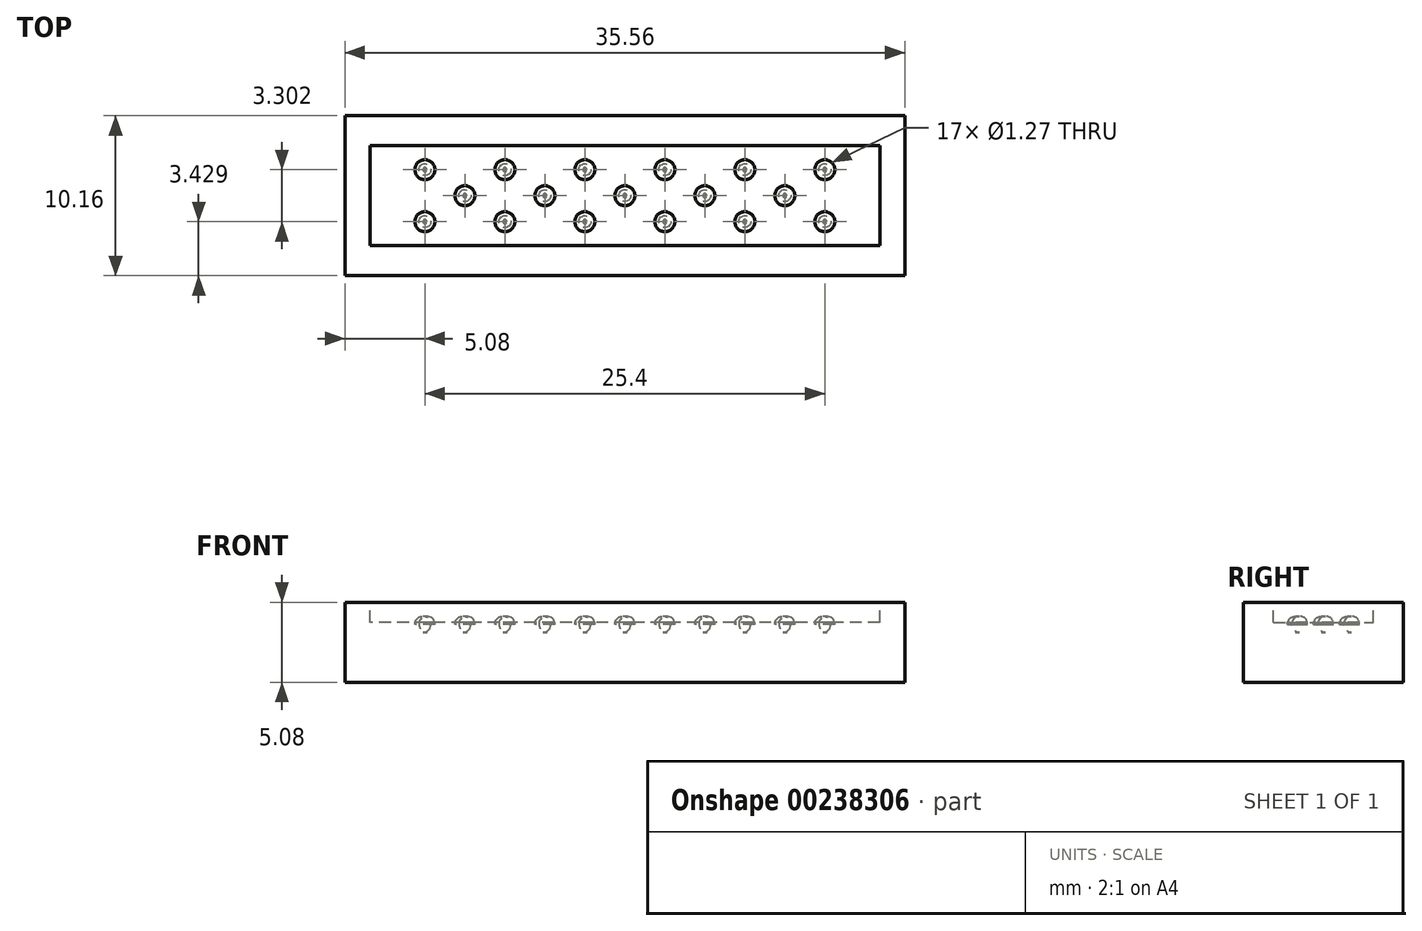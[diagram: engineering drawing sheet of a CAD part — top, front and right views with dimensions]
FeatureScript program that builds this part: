
annotation { "Feature Type Name" : "Feature", "Feature Type Description" : "" }
export const myFeature = defineFeature(function(context is Context, id is Id, definition is map)
    precondition{}
    {
        {
            var Q0;
            Q0=qCreatedBy(makeId("Top.planeOp"),FACE);
            var sketch = newSketch(context, id + "F0", { "sketchPlane" : qUnion([Q0])});
            skLineSegment(sketch, "E0.bottom", {"start": v(17.78, -5.08) * mm, "end": v(-17.78, -5.08) * mm});
            skLineSegment(sketch, "E0.top", {"start": v(17.78, 5.08) * mm, "end": v(-17.78, 5.08) * mm});
            skLineSegment(sketch, "E0.left", {"start": v(17.78, -5.08) * mm, "end": v(17.78, 5.08) * mm});
            skLineSegment(sketch, "E0.right", {"start": v(-17.78, -5.08) * mm, "end": v(-17.78, 5.08) * mm});
            skPoint(sketch, "E0.middle", {"position": v(0, 0) * mm});
            skSolve(sketch);
        }
        {
            var Q0;
            Q0=makeQuery(id+"F0.imprint","IMPRINT",FACE,{"disambiguationData":[TD([[makeQuery(id+"F0.imprint","IMPRINT",EDGE,{"derivedFrom":sQuery(id+"F0.wireOp",EDGE,"E0.bottom")}),-1.0]])]});
            extrude(context, id + "F1", {"entities" : qUnion([Q0]), "depth" : 5.08 * mm});
        }
        {
            var Q0;
            Q0=makeQuery(id+"F1.opExtrude","CAP_FACE",FACE,{"disambiguationData":[OSD([sQuery(id+"F0.wireOp",EDGE,"E0.bottom"),sQuery(id+"F0.wireOp",EDGE,"E0.top"),sQuery(id+"F0.wireOp",EDGE,"E0.left"),sQuery(id+"F0.wireOp",EDGE,"E0.right")])],"isStart":false});
            var sketch = newSketch(context, id + "F2", { "sketchPlane" : qUnion([Q0])});
            skLineSegment(sketch, "E1.bottom", {"start": v(16.2, -3.18) * mm, "end": v(-16.2, -3.18) * mm});
            skLineSegment(sketch, "E1.top", {"start": v(16.2, 3.18) * mm, "end": v(-16.2, 3.18) * mm});
            skLineSegment(sketch, "E1.left", {"start": v(16.2, -3.18) * mm, "end": v(16.2, 3.17) * mm});
            skLineSegment(sketch, "E1.right", {"start": v(-16.2, -3.18) * mm, "end": v(-16.2, 3.17) * mm});
            skPoint(sketch, "E1.middle", {"position": v(0, 0) * mm});
            skSolve(sketch);
        }
        {
            var Q0;
            Q0 = qSketchRegion(id + "F2", true);
            extrude(context, id + "F3", {"entities" : qUnion([Q0]), "operationType" : NewBodyOperationType.REMOVE, "oppositeDirection" : true, "depth" : 1.27 * mm});
        }
        {
            var Q0;
            Q0=makeQuery(id+"F3.boolean.opBoolean","COPY",FACE,{"derivedFrom":makeQuery(id+"F3.opExtrude","CAP_FACE",FACE,{"disambiguationData":[OSD([sQuery(id+"F2.wireOp",EDGE,"E1.bottom"),sQuery(id+"F2.wireOp",EDGE,"E1.top"),sQuery(id+"F2.wireOp",EDGE,"E1.left"),sQuery(id+"F2.wireOp",EDGE,"E1.right")])],"isStart":false})});
            var sketch = newSketch(context, id + "F4", { "sketchPlane" : qUnion([Q0])});
            skCircle(sketch, "E2", {"center": v(-12.7, 1.65) * mm, "radius": 0.64 * mm});
            skCircle(sketch, "E3", {"center": v(-10.16, 0) * mm, "radius": 0.64 * mm});
            skCircle(sketch, "E4.1.0.0", {"center": v(-7.62, 1.65) * mm, "radius": 0.64 * mm});
            skCircle(sketch, "E4.2.0.0", {"center": v(-2.54, 1.65) * mm, "radius": 0.64 * mm});
            skCircle(sketch, "E4.3.0.0", {"center": v(2.54, 1.65) * mm, "radius": 0.64 * mm});
            skCircle(sketch, "E4.4.0.0", {"center": v(7.62, 1.65) * mm, "radius": 0.64 * mm});
            skCircle(sketch, "E4.5.0.0", {"center": v(12.7, 1.65) * mm, "radius": 0.64 * mm});
            skLineSegment(sketch, "E4.direction1", {"start": v(-12.7, 1.65) * mm, "end": v(-7.62, 1.65) * mm, "construction": true});
            skLineSegment(sketch, "E5", {"start": v(-2.54, 1.65) * mm, "end": v(2.54, 1.65) * mm, "construction": true});
            skPoint(sketch, "E6", {"position": v(0, 1.65) * mm});
            skCircle(sketch, "E7.1.0.0", {"center": v(-5.08, 0) * mm, "radius": 0.64 * mm});
            skCircle(sketch, "E7.2.0.0", {"center": v(0, 0) * mm, "radius": 0.64 * mm});
            skCircle(sketch, "E7.3.0.0", {"center": v(5.08, 0) * mm, "radius": 0.64 * mm});
            skCircle(sketch, "E7.4.0.0", {"center": v(10.16, 0) * mm, "radius": 0.64 * mm});
            skLineSegment(sketch, "E7.direction1", {"start": v(-10.16, 0) * mm, "end": v(-5.08, 0) * mm, "construction": true});
            skCircle(sketch, "E8.MirrorC", {"center": v(-12.7, -1.65) * mm, "radius": 0.64 * mm});
            skCircle(sketch, "E9.MirrorC", {"center": v(-7.62, -1.65) * mm, "radius": 0.64 * mm});
            skCircle(sketch, "E10.MirrorC", {"center": v(-2.54, -1.65) * mm, "radius": 0.64 * mm});
            skCircle(sketch, "E11.MirrorC", {"center": v(2.54, -1.65) * mm, "radius": 0.64 * mm});
            skCircle(sketch, "E12.MirrorC", {"center": v(7.62, -1.65) * mm, "radius": 0.64 * mm});
            skCircle(sketch, "E13.MirrorC", {"center": v(12.7, -1.65) * mm, "radius": 0.64 * mm});
            skSolve(sketch);
        }
        {
            var Q0;
            Q0 = qSketchRegion(id + "F4", true);
            extrude(context, id + "F5", {"entities" : qUnion([Q0]), "operationType" : NewBodyOperationType.REMOVE, "oppositeDirection" : true, "depth" : 0.64 * mm});
        }
        {
            var Q0;
            Q0=makeQuery(id+"F5.boolean.opBoolean","COPY",EDGE,{"derivedFrom":makeQuery(id+"F5.opExtrude","CAP_EDGE",EDGE,{"disambiguationData":[OSD([sQuery(id+"F4.wireOp",EDGE,"E2")])],"isStart":false})});
            var Q1;
            Q1=makeQuery(id+"F5.boolean.opBoolean","COPY",EDGE,{"derivedFrom":makeQuery(id+"F5.opExtrude","CAP_EDGE",EDGE,{"disambiguationData":[OSD([sQuery(id+"F4.wireOp",EDGE,"E8.MirrorC")])],"isStart":false})});
            var Q2;
            Q2=makeQuery(id+"F5.boolean.opBoolean","COPY",EDGE,{"derivedFrom":makeQuery(id+"F5.opExtrude","CAP_EDGE",EDGE,{"disambiguationData":[OSD([sQuery(id+"F4.wireOp",EDGE,"E3")])],"isStart":false})});
            var Q3;
            Q3=makeQuery(id+"F5.boolean.opBoolean","COPY",EDGE,{"derivedFrom":makeQuery(id+"F5.opExtrude","CAP_EDGE",EDGE,{"disambiguationData":[OSD([sQuery(id+"F4.wireOp",EDGE,"E4.1.0.0")])],"isStart":false})});
            var Q4;
            Q4=makeQuery(id+"F5.boolean.opBoolean","COPY",EDGE,{"derivedFrom":makeQuery(id+"F5.opExtrude","CAP_EDGE",EDGE,{"disambiguationData":[OSD([sQuery(id+"F4.wireOp",EDGE,"E7.1.0.0")])],"isStart":false})});
            var Q5;
            Q5=makeQuery(id+"F5.boolean.opBoolean","COPY",EDGE,{"derivedFrom":makeQuery(id+"F5.opExtrude","CAP_EDGE",EDGE,{"disambiguationData":[OSD([sQuery(id+"F4.wireOp",EDGE,"E4.2.0.0")])],"isStart":false})});
            var Q6;
            Q6=makeQuery(id+"F5.boolean.opBoolean","COPY",EDGE,{"derivedFrom":makeQuery(id+"F5.opExtrude","CAP_EDGE",EDGE,{"disambiguationData":[OSD([sQuery(id+"F4.wireOp",EDGE,"E10.MirrorC")])],"isStart":false})});
            var Q7;
            Q7=makeQuery(id+"F5.boolean.opBoolean","COPY",EDGE,{"derivedFrom":makeQuery(id+"F5.opExtrude","CAP_EDGE",EDGE,{"disambiguationData":[OSD([sQuery(id+"F4.wireOp",EDGE,"E9.MirrorC")])],"isStart":false})});
            var Q8;
            Q8=makeQuery(id+"F5.boolean.opBoolean","COPY",EDGE,{"derivedFrom":makeQuery(id+"F5.opExtrude","CAP_EDGE",EDGE,{"disambiguationData":[OSD([sQuery(id+"F4.wireOp",EDGE,"E7.2.0.0")])],"isStart":false})});
            var Q9;
            Q9=makeQuery(id+"F5.boolean.opBoolean","COPY",EDGE,{"derivedFrom":makeQuery(id+"F5.opExtrude","CAP_EDGE",EDGE,{"disambiguationData":[OSD([sQuery(id+"F4.wireOp",EDGE,"E4.3.0.0")])],"isStart":false})});
            var Q10;
            Q10=makeQuery(id+"F5.boolean.opBoolean","COPY",EDGE,{"derivedFrom":makeQuery(id+"F5.opExtrude","CAP_EDGE",EDGE,{"disambiguationData":[OSD([sQuery(id+"F4.wireOp",EDGE,"E11.MirrorC")])],"isStart":false})});
            var Q11;
            Q11=makeQuery(id+"F5.boolean.opBoolean","COPY",EDGE,{"derivedFrom":makeQuery(id+"F5.opExtrude","CAP_EDGE",EDGE,{"disambiguationData":[OSD([sQuery(id+"F4.wireOp",EDGE,"E7.3.0.0")])],"isStart":false})});
            var Q12;
            Q12=makeQuery(id+"F5.boolean.opBoolean","COPY",EDGE,{"derivedFrom":makeQuery(id+"F5.opExtrude","CAP_EDGE",EDGE,{"disambiguationData":[OSD([sQuery(id+"F4.wireOp",EDGE,"E12.MirrorC")])],"isStart":false})});
            var Q13;
            Q13=makeQuery(id+"F5.boolean.opBoolean","COPY",EDGE,{"derivedFrom":makeQuery(id+"F5.opExtrude","CAP_EDGE",EDGE,{"disambiguationData":[OSD([sQuery(id+"F4.wireOp",EDGE,"E4.4.0.0")])],"isStart":false})});
            var Q14;
            Q14=makeQuery(id+"F5.boolean.opBoolean","COPY",EDGE,{"derivedFrom":makeQuery(id+"F5.opExtrude","CAP_EDGE",EDGE,{"disambiguationData":[OSD([sQuery(id+"F4.wireOp",EDGE,"E7.4.0.0")])],"isStart":false})});
            var Q15;
            Q15=makeQuery(id+"F5.boolean.opBoolean","COPY",EDGE,{"derivedFrom":makeQuery(id+"F5.opExtrude","CAP_EDGE",EDGE,{"disambiguationData":[OSD([sQuery(id+"F4.wireOp",EDGE,"E4.5.0.0")])],"isStart":false})});
            var Q16;
            Q16=makeQuery(id+"F5.boolean.opBoolean","COPY",EDGE,{"derivedFrom":makeQuery(id+"F5.opExtrude","CAP_EDGE",EDGE,{"disambiguationData":[OSD([sQuery(id+"F4.wireOp",EDGE,"E13.MirrorC")])],"isStart":false})});
            fillet(context, id + "F6", {"entities" : qUnion([Q0, Q1, Q2, Q3, Q4, Q5, Q6, Q7, Q8, Q9, Q10, Q11, Q12, Q13, Q14, Q15, Q16]), "radius" : 0.5 * mm, "tangentPropagation" : true, "allowEdgeOverflow" : false});
        }
    });
